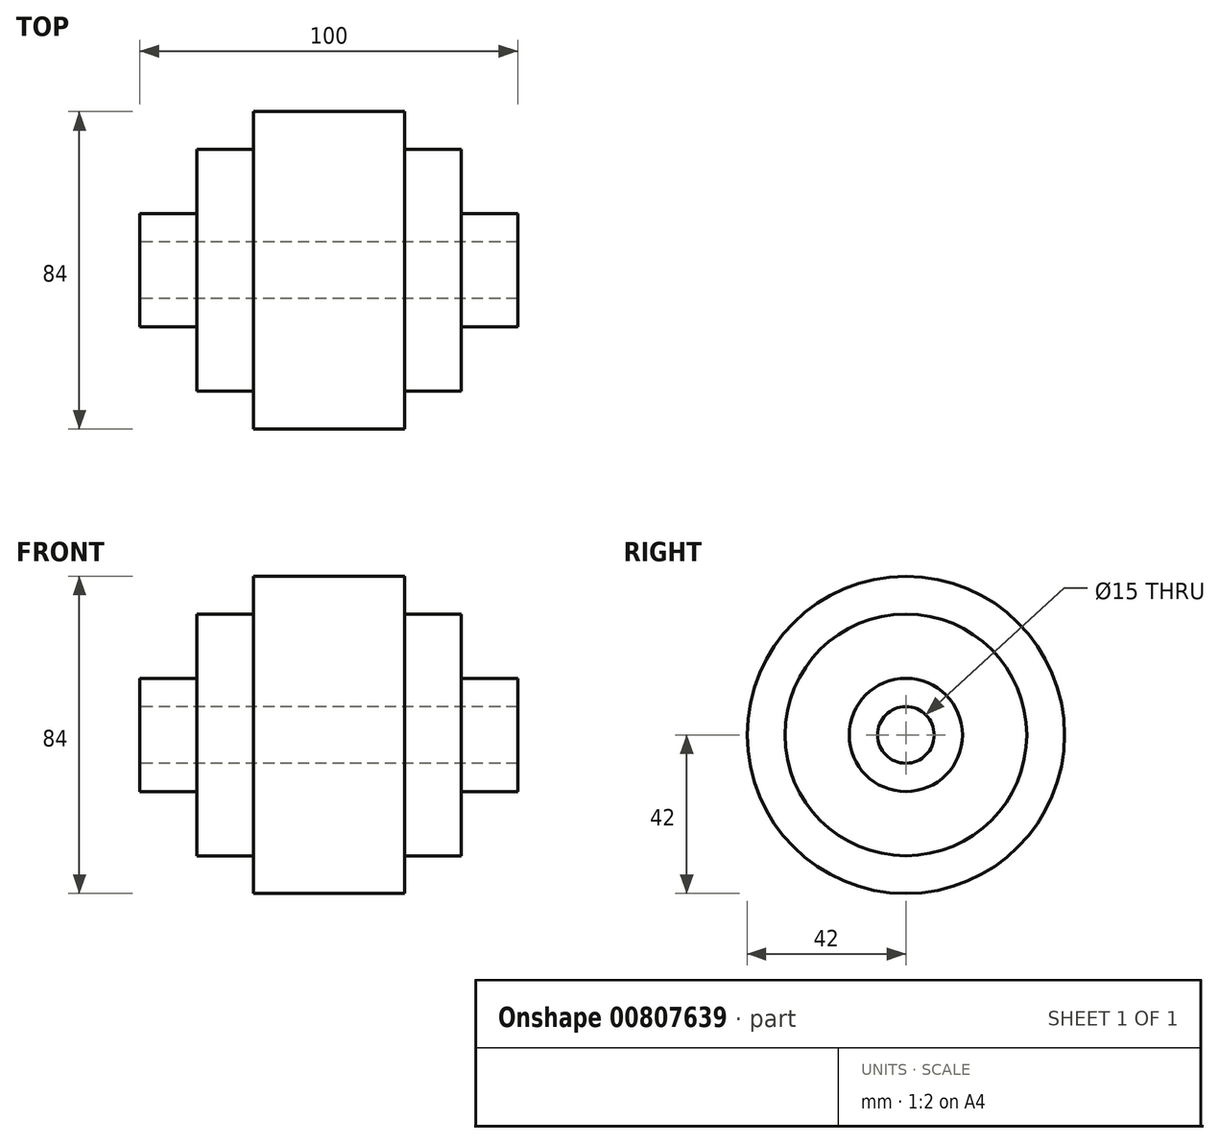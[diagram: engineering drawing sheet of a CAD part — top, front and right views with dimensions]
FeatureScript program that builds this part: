
annotation { "Feature Type Name" : "Feature", "Feature Type Description" : "" }
export const myFeature = defineFeature(function(context is Context, id is Id, definition is map)
    precondition{}
    {
        {
            var Q0;
            Q0=qCreatedBy(makeId("Top.planeOp"),FACE);
            var sketch = newSketch(context, id + "F0", { "sketchPlane" : qUnion([Q0])});
            skLineSegment(sketch, "E0.bottom", {"start": v(-50, 15) * mm, "end": v(-35, 15) * mm});
            skLineSegment(sketch, "E0.top", {"start": v(-50, 0) * mm, "end": v(50, 0) * mm});
            skLineSegment(sketch, "E0.left", {"start": v(-50, 15) * mm, "end": v(-50, 7.5) * mm});
            skLineSegment(sketch, "E0.right", {"start": v(50, 15) * mm, "end": v(50, 7.5) * mm});
            skLineSegment(sketch, "E1.top", {"start": v(-35, 32) * mm, "end": v(-20, 32) * mm});
            skLineSegment(sketch, "E1.left", {"start": v(-35, 15) * mm, "end": v(-35, 32) * mm});
            skLineSegment(sketch, "E1.right", {"start": v(35, 15) * mm, "end": v(35, 32) * mm});
            skLineSegment(sketch, "E2.top", {"start": v(-20, 42) * mm, "end": v(20, 42) * mm});
            skLineSegment(sketch, "E2.left", {"start": v(-20, 32) * mm, "end": v(-20, 42) * mm});
            skLineSegment(sketch, "E2.right", {"start": v(20, 32) * mm, "end": v(20, 42) * mm});
            skLineSegment(sketch, "E3.trimOffspring", {"start": v(20, 32) * mm, "end": v(35, 32) * mm});
            skLineSegment(sketch, "E4.trimOffspring", {"start": v(35, 15) * mm, "end": v(50, 15) * mm});
            skLineSegment(sketch, "E5", {"start": v(148.63, 0) * mm, "end": v(-112.82, 0) * mm, "construction": true});
            skLineSegment(sketch, "E6.bottom", {"start": v(50, 0) * mm, "end": v(-50, 0) * mm});
            skLineSegment(sketch, "E6.top", {"start": v(50, 7.5) * mm, "end": v(-50, 7.5) * mm});
            skSolve(sketch);
        }
        {
            var Q0;
            Q0 = qSketchRegion(id + "F0", true);
            var Q1;
            Q1=sQuery(id+"F0.wireOp",EDGE,"E0.top");
            revolve(context, id + "F1", {"surfaceOperationType" : NewSurfaceOperationType.NEW, "entities" : qUnion([Q0]), "axis" : qUnion([Q1]), "revolveType" : RevolveType.FULL});
        }
    });
